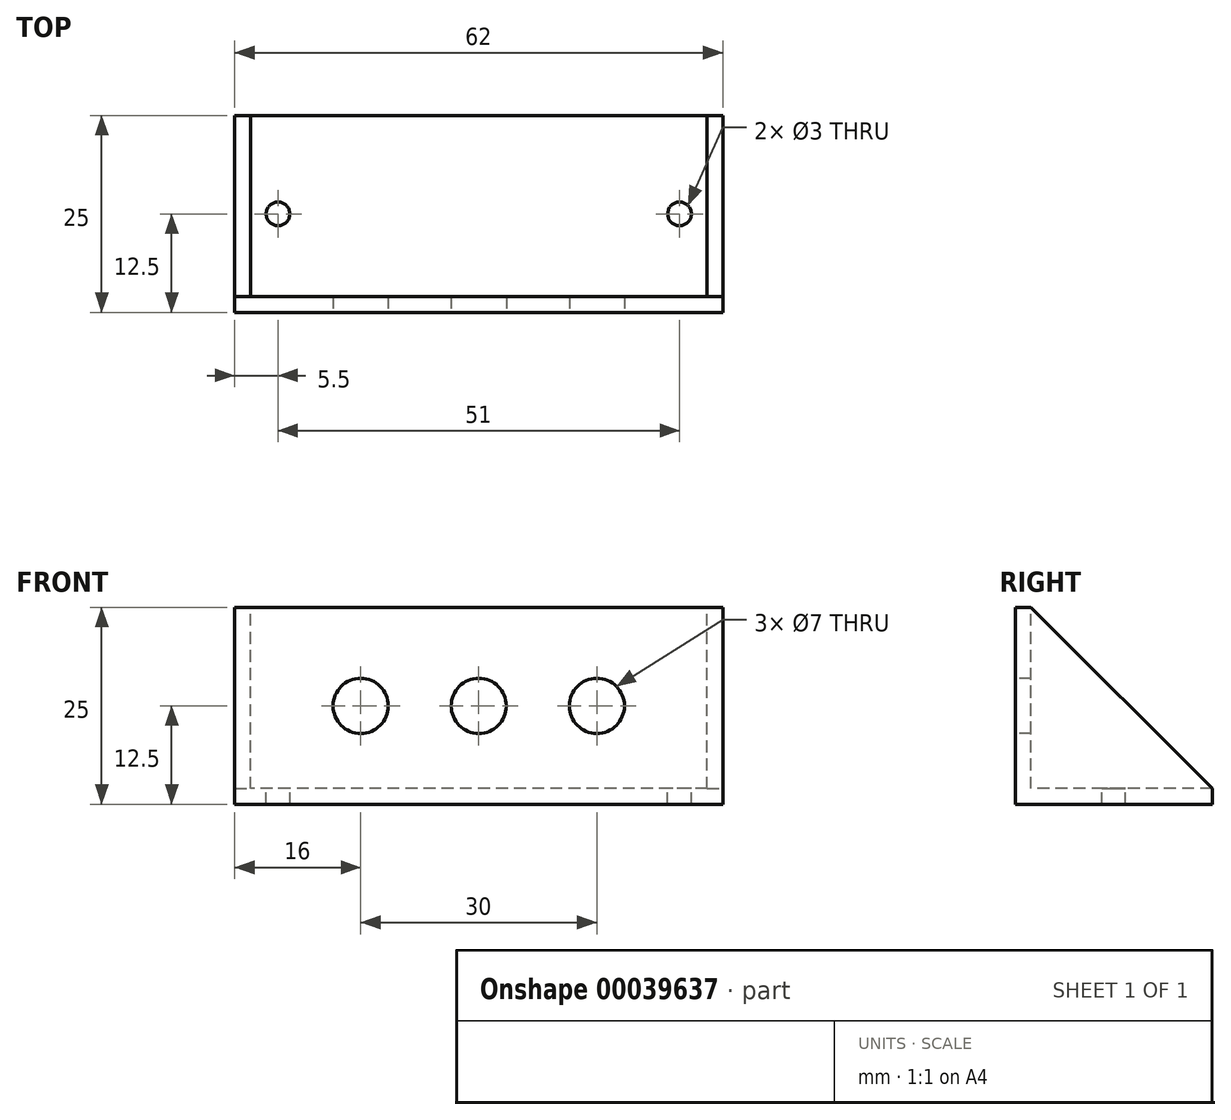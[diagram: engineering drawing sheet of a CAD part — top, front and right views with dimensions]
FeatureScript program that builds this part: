
annotation { "Feature Type Name" : "Feature", "Feature Type Description" : "" }
export const myFeature = defineFeature(function(context is Context, id is Id, definition is map)
    precondition{}
    {
        {
            var Q0;
            Q0=qCreatedBy(makeId("Top.planeOp"),FACE);
            var sketch = newSketch(context, id + "F0", { "sketchPlane" : qUnion([Q0])});
            skLineSegment(sketch, "E0.rect.bottom", {"start": v(31, -12.5) * mm, "end": v(-31, -12.5) * mm});
            skLineSegment(sketch, "E0.rect.top", {"start": v(31, 12.5) * mm, "end": v(-31, 12.5) * mm});
            skLineSegment(sketch, "E0.rect.left", {"start": v(31, -12.5) * mm, "end": v(31, 12.5) * mm});
            skLineSegment(sketch, "E0.rect.right", {"start": v(-31, -12.5) * mm, "end": v(-31, 12.5) * mm});
            skPoint(sketch, "E0.rect.middle", {"position": v(0, 0) * mm});
            skSolve(sketch);
        }
        {
            var Q0;
            Q0 = qSketchRegion(id + "F0", true);
            extrude(context, id + "F1", {"entities" : qUnion([Q0]), "depth" : 25 * mm});
        }
        {
            var Q0;
            Q0=makeQuery(id+"F1.opExtrude","SWEPT_FACE",FACE,{"disambiguationData":[OSD([sQuery(id+"F0.wireOp",EDGE,"E0.rect.bottom")])]});
            var sketch = newSketch(context, id + "F2", { "sketchPlane" : qUnion([Q0])});
            skLineSegment(sketch, "E1", {"start": v(-31, 12.5) * mm, "end": v(31, 12.5) * mm, "construction": true});
            skLineSegment(sketch, "E2", {"start": v(0, 25) * mm, "end": v(0, 0) * mm, "construction": true});
            skCircle(sketch, "E3", {"center": v(0, 12.5) * mm, "radius": 3.5 * mm});
            skCircle(sketch, "E4", {"center": v(-15, 12.5) * mm, "radius": 3.5 * mm});
            skCircle(sketch, "E5", {"center": v(15, 12.5) * mm, "radius": 3.5 * mm});
            skSolve(sketch);
        }
        {
            var Q0;
            Q0 = qSketchRegion(id + "F2", true);
            extrude(context, id + "F3", {"entities" : qUnion([Q0]), "operationType" : NewBodyOperationType.REMOVE, "oppositeDirection" : true, "depth" : 25 * mm});
        }
        {
            var Q0;
            Q0=makeQuery(id+"F1.opExtrude","CAP_FACE",FACE,{"disambiguationData":[OSD([sQuery(id+"F0.wireOp",EDGE,"E0.rect.bottom"),sQuery(id+"F0.wireOp",EDGE,"E0.rect.top"),sQuery(id+"F0.wireOp",EDGE,"E0.rect.left"),sQuery(id+"F0.wireOp",EDGE,"E0.rect.right")])],"isStart":false});
            var sketch = newSketch(context, id + "F4", { "sketchPlane" : qUnion([Q0])});
            skLineSegment(sketch, "E6.bottom", {"start": v(-29, 12.5) * mm, "end": v(29, 12.5) * mm});
            skLineSegment(sketch, "E6.top", {"start": v(-29, -10.5) * mm, "end": v(29, -10.5) * mm});
            skLineSegment(sketch, "E6.left", {"start": v(-29, 12.5) * mm, "end": v(-29, -10.5) * mm});
            skLineSegment(sketch, "E6.right", {"start": v(29, 12.5) * mm, "end": v(29, -10.5) * mm});
            skSolve(sketch);
        }
        {
            var Q0;
            Q0 = qSketchRegion(id + "F4", true);
            extrude(context, id + "F5", {"entities" : qUnion([Q0]), "operationType" : NewBodyOperationType.REMOVE, "oppositeDirection" : true, "depth" : 23 * mm});
        }
        {
            var Q0;
            Q0=makeQuery(id+"F1.opExtrude","SWEPT_FACE",FACE,{"disambiguationData":[OSD([sQuery(id+"F0.wireOp",EDGE,"E0.rect.left")])]});
            var sketch = newSketch(context, id + "F6", { "sketchPlane" : qUnion([Q0])});
            skLineSegment(sketch, "E7", {"start": v(-10.5, 25) * mm, "end": v(12.5, 2) * mm});
            skLineSegment(sketch, "E8", {"start": v(12.5, 2) * mm, "end": v(12.5, 25) * mm});
            skLineSegment(sketch, "E9", {"start": v(12.5, 25) * mm, "end": v(-10.5, 25) * mm});
            skSolve(sketch);
        }
        {
            var Q0;
            Q0 = qSketchRegion(id + "F6", true);
            extrude(context, id + "F7", {"entities" : qUnion([Q0]), "operationType" : NewBodyOperationType.REMOVE, "endBound" : BoundingType.THROUGH_ALL, "oppositeDirection" : true, "depth" : 25 * mm});
        }
        {
            var Q0;
            Q0=makeQuery(id+"F5.boolean.opBoolean","COPY",FACE,{"derivedFrom":makeQuery(id+"F5.opExtrude","CAP_FACE",FACE,{"disambiguationData":[OSD([sQuery(id+"F4.wireOp",EDGE,"E6.bottom"),sQuery(id+"F4.wireOp",EDGE,"E6.top"),sQuery(id+"F4.wireOp",EDGE,"E6.left"),sQuery(id+"F4.wireOp",EDGE,"E6.right")])],"isStart":false})});
            var sketch = newSketch(context, id + "F8", { "sketchPlane" : qUnion([Q0])});
            skCircle(sketch, "E10", {"center": v(-25.5, 0) * mm, "radius": 1.5 * mm});
            skCircle(sketch, "E11", {"center": v(25.5, 0) * mm, "radius": 1.5 * mm});
            skSolve(sketch);
        }
        {
            var Q0;
            Q0 = qSketchRegion(id + "F8", true);
            extrude(context, id + "F9", {"entities" : qUnion([Q0]), "operationType" : NewBodyOperationType.REMOVE, "endBound" : BoundingType.THROUGH_ALL, "oppositeDirection" : true, "depth" : 25 * mm});
        }
    });
